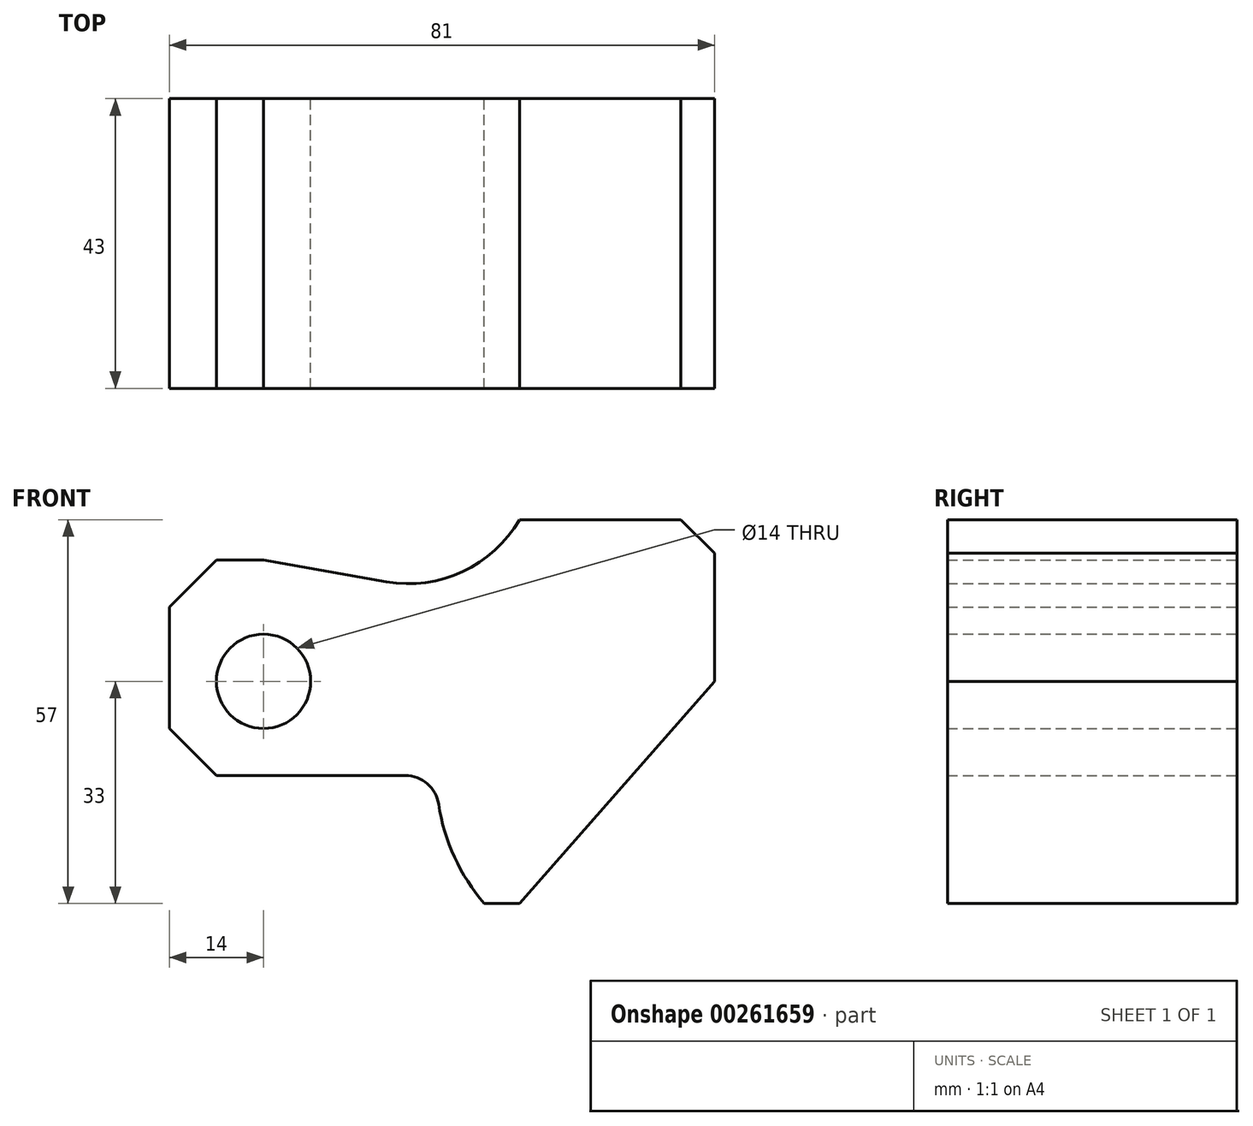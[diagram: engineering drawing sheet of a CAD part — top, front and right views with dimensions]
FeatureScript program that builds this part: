
annotation { "Feature Type Name" : "Feature", "Feature Type Description" : "" }
export const myFeature = defineFeature(function(context is Context, id is Id, definition is map)
    precondition{}
    {
        {
            var Q0;
            Q0=qCreatedBy(makeId("Front.planeOp"),FACE);
            var sketch = newSketch(context, id + "F0", { "sketchPlane" : qUnion([Q0])});
            skCircle(sketch, "E0", {"center": v(0, 0) * mm, "radius": 7 * mm});
            skLineSegment(sketch, "E1", {"start": v(0, 0) * mm, "end": v(-14, 0) * mm});
            skLineSegment(sketch, "E2", {"start": v(-14, 0) * mm, "end": v(-14, 11) * mm});
            skLineSegment(sketch, "E3", {"start": v(-14, 0) * mm, "end": v(-14, -7) * mm});
            skLineSegment(sketch, "E4", {"start": v(-14, 11) * mm, "end": v(-7, 18) * mm});
            skLineSegment(sketch, "E5", {"start": v(-7, 18) * mm, "end": v(0, 18) * mm});
            skLineSegment(sketch, "E6", {"start": v(-7, -14) * mm, "end": v(-14, -7) * mm});
            skLineSegment(sketch, "E7", {"start": v(-7, -14) * mm, "end": v(0, -14) * mm});
            skLineSegment(sketch, "E8", {"start": v(0, 18) * mm, "end": v(19.04, 18) * mm, "construction": true});
            skLineSegment(sketch, "E9", {"start": v(0, 18) * mm, "end": v(18.24, 14.78) * mm});
            skLineSegment(sketch, "E10", {"start": v(0, -14) * mm, "end": v(16.49, -14) * mm});
            skLineSegment(sketch, "E11", {"start": v(0, 0) * mm, "end": v(7, 0) * mm});
            skLineSegment(sketch, "E12", {"start": v(67, 0) * mm, "end": v(67, 19) * mm});
            skLineSegment(sketch, "E13", {"start": v(67, 19) * mm, "end": v(62, 24) * mm});
            skLineSegment(sketch, "E14", {"start": v(67, 19) * mm, "end": v(67, 30.65) * mm, "construction": true});
            skLineSegment(sketch, "E15", {"start": v(62, 24) * mm, "end": v(38, 24) * mm});
            skArc(sketch, "E16", {"start": v(18.24, 14.78) * mm, "mid": v(29.57, 16.28) * mm, "end": v(38, 24) * mm});
            skLineSegment(sketch, "E17", {"start": v(67, 0) * mm, "end": v(67, -33) * mm, "construction": true});
            skLineSegment(sketch, "E18", {"start": v(67, -33) * mm, "end": v(38, -33) * mm, "construction": true});
            skLineSegment(sketch, "E19", {"start": v(38, -33) * mm, "end": v(67, 0) * mm});
            skLineSegment(sketch, "E20", {"start": v(16.49, -14) * mm, "end": v(21.07, -14) * mm, "construction": true});
            skLineSegment(sketch, "E21", {"start": v(38, -33) * mm, "end": v(32.79, -33) * mm});
            skLineSegment(sketch, "E22", {"start": v(7, 0) * mm, "end": v(67, 0) * mm});
            skArc(sketch, "E23", {"start": v(26.01, -18.26) * mm, "mid": v(28.35, -26.12) * mm, "end": v(32.79, -33) * mm});
            skLineSegment(sketch, "E24", {"start": v(16.49, -14) * mm, "end": v(21.07, -14) * mm});
            skArc(sketch, "E25.filletArc", {"start": v(26.01, -18.26) * mm, "mid": v(24.33, -15.21) * mm, "end": v(21.07, -14) * mm});
            skSolve(sketch);
        }
        {
            var Q0;
            Q0 = qSketchRegion(id + "F0", true);
            extrude(context, id + "F1", {"entities" : qUnion([Q0]), "depth" : 43 * mm});
        }
    });
